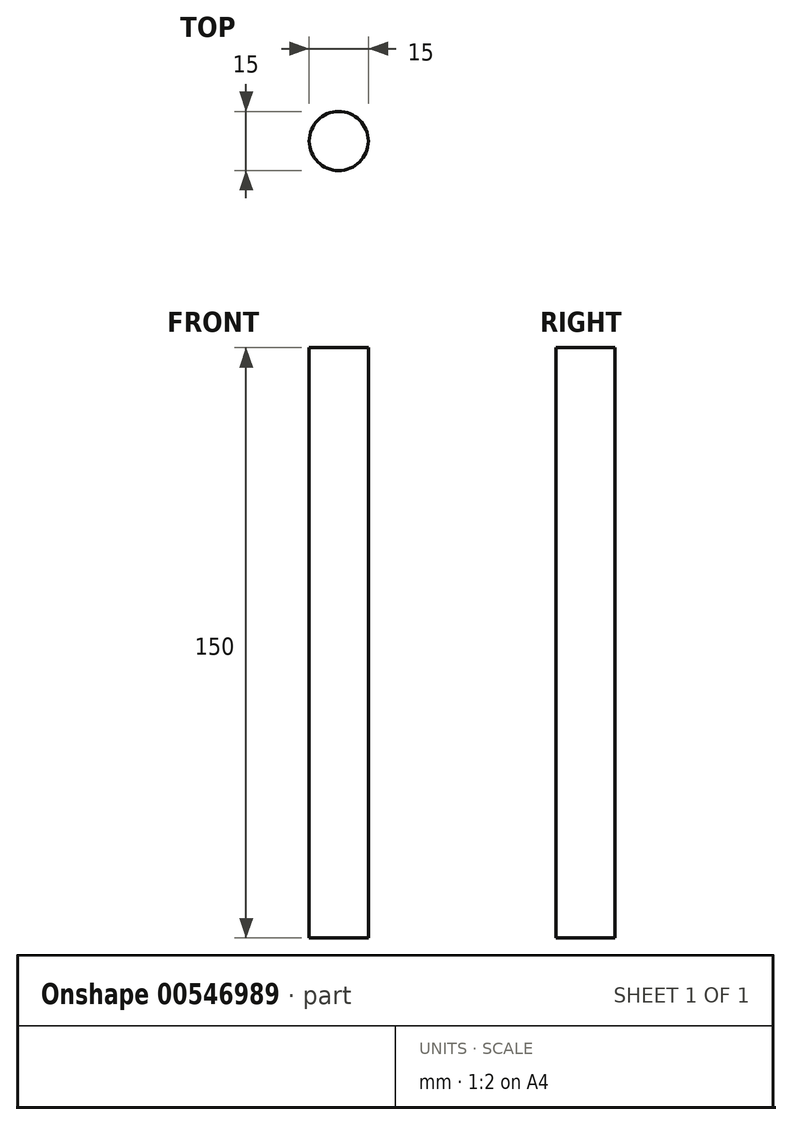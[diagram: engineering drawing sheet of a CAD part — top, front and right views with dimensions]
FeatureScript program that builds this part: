
annotation { "Feature Type Name" : "Feature", "Feature Type Description" : "" }
export const myFeature = defineFeature(function(context is Context, id is Id, definition is map)
    precondition{}
    {
        {
            var Q0;
            Q0=qCreatedBy(makeId("Top.planeOp"),FACE);
            var sketch = newSketch(context, id + "F0", { "sketchPlane" : qUnion([Q0])});
            skCircle(sketch, "E0", {"center": v(0, 0) * mm, "radius": 7.5 * mm});
            skSolve(sketch);
        }
        {
            var Q0;
            Q0=makeQuery(id+"F0.imprint","IMPRINT",FACE,{"disambiguationData":[TD([[makeQuery(id+"F0.imprint","IMPRINT",EDGE,{"derivedFrom":sQuery(id+"F0.wireOp",EDGE,"E0")}),1.0]])]});
            extrude(context, id + "F1", {"entities" : qUnion([Q0]), "depth" : 150 * mm, "offsetDistance" : 25 * mm});
        }
    });
